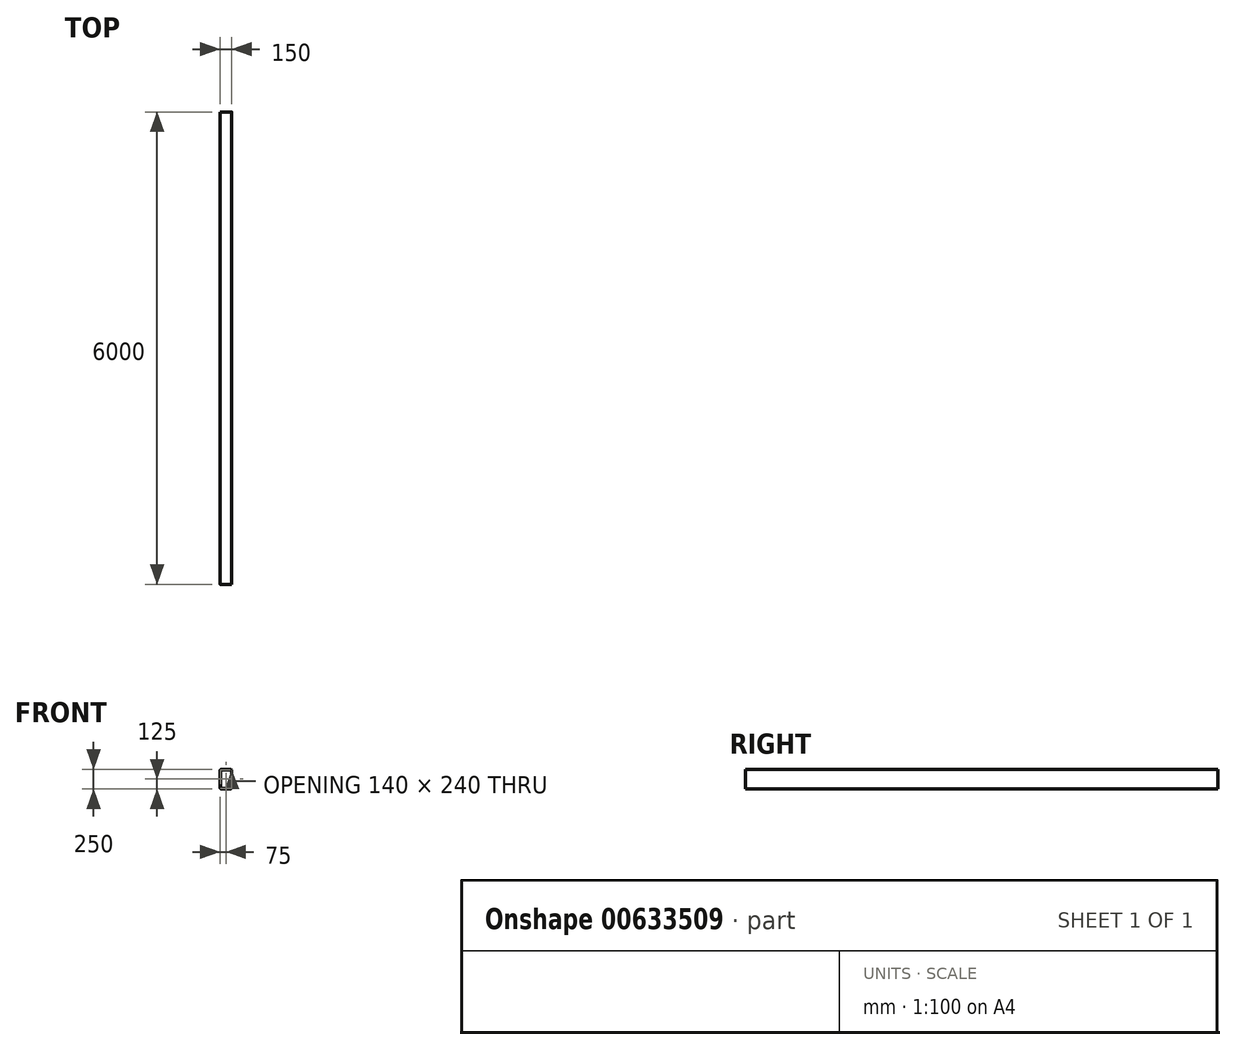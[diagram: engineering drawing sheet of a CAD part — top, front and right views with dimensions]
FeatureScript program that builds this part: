
annotation { "Feature Type Name" : "Feature", "Feature Type Description" : "" }
export const myFeature = defineFeature(function(context is Context, id is Id, definition is map)
    precondition{}
    {
        {
            var Q0;
            Q0=qCreatedBy(makeId("Front.planeOp"),FACE);
            var sketch = newSketch(context, id + "F0", { "sketchPlane" : qUnion([Q0])});
            skLineSegment(sketch, "E0.bottom", {"start": v(18, 0) * mm, "end": v(132, 0) * mm});
            skLineSegment(sketch, "E0.top", {"start": v(18, -250) * mm, "end": v(132, -250) * mm});
            skLineSegment(sketch, "E0.left", {"start": v(0, -18) * mm, "end": v(0, -232) * mm});
            skLineSegment(sketch, "E0.right", {"start": v(150, -18) * mm, "end": v(150, -232) * mm});
            skPoint(sketch, "E1.visualSharp", {"position": v(150, 0) * mm});
            skArc(sketch, "E1.filletArc", {"start": v(150, -18) * mm, "mid": v(144.73, -5.27) * mm, "end": v(132, 0) * mm});
            skPoint(sketch, "E2.visualSharp", {"position": v(0, 0) * mm});
            skArc(sketch, "E2.filletArc", {"start": v(18, 0) * mm, "mid": v(5.27, -5.27) * mm, "end": v(0, -18) * mm});
            skPoint(sketch, "E3.visualSharp", {"position": v(0, -250) * mm});
            skArc(sketch, "E3.filletArc", {"start": v(0, -232) * mm, "mid": v(5.27, -244.73) * mm, "end": v(18, -250) * mm});
            skPoint(sketch, "E4.visualSharp", {"position": v(150, -250) * mm});
            skArc(sketch, "E4.filletArc", {"start": v(132, -250) * mm, "mid": v(144.73, -244.73) * mm, "end": v(150, -232) * mm});
            skArc(sketch, "E5.0", {"start": v(18, -5) * mm, "mid": v(8.8, -8.8) * mm, "end": v(5, -18) * mm});
            skLineSegment(sketch, "E5.1", {"start": v(5, -18) * mm, "end": v(5, -232) * mm});
            skLineSegment(sketch, "E5.2", {"start": v(18, -5) * mm, "end": v(132, -5) * mm});
            skArc(sketch, "E5.3", {"start": v(5, -232) * mm, "mid": v(8.8, -241.2) * mm, "end": v(18, -245) * mm});
            skArc(sketch, "E5.4", {"start": v(145, -18) * mm, "mid": v(141.2, -8.8) * mm, "end": v(132, -5) * mm});
            skLineSegment(sketch, "E5.5", {"start": v(145, -18) * mm, "end": v(145, -232) * mm});
            skArc(sketch, "E5.6", {"start": v(132, -245) * mm, "mid": v(141.2, -241.2) * mm, "end": v(145, -232) * mm});
            skLineSegment(sketch, "E5.7", {"start": v(18, -245) * mm, "end": v(132, -245) * mm});
            skSolve(sketch);
        }
        {
            var Q0;
            Q0 = qSketchRegion(id + "F0", true);
            extrude(context, id + "F1", {"entities" : qUnion([Q0]), "depth" : 6000 * mm, "offsetDistance" : 25 * mm});
        }
    });
